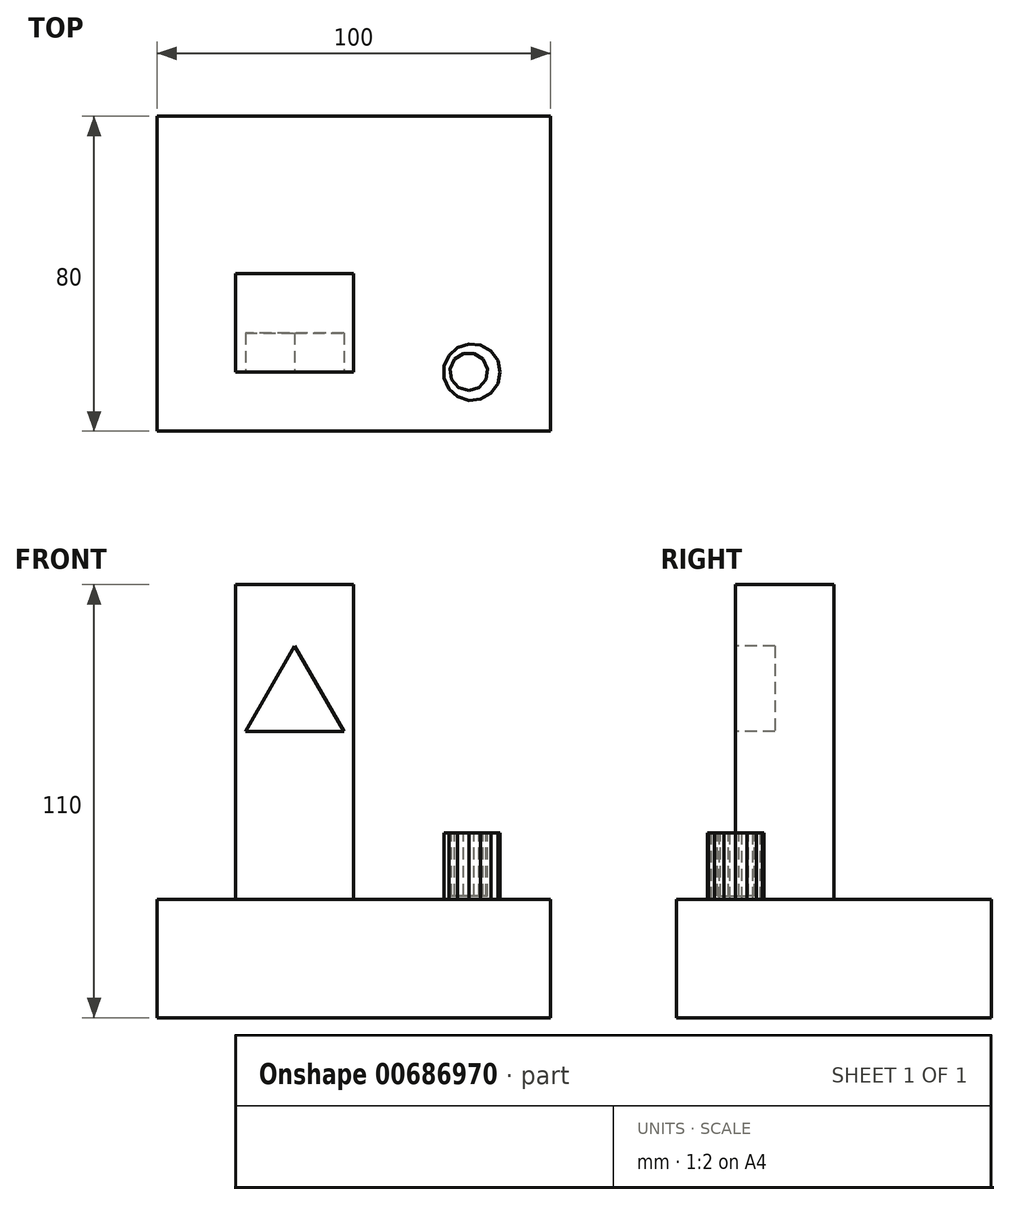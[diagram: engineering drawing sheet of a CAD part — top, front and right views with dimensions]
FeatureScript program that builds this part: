
annotation { "Feature Type Name" : "Feature", "Feature Type Description" : "" }
export const myFeature = defineFeature(function(context is Context, id is Id, definition is map)
    precondition{}
    {
        {
            var Q0;
            Q0=qCreatedBy(makeId("Top.planeOp"),FACE);
            var sketch = newSketch(context, id + "F0", { "sketchPlane" : qUnion([Q0])});
            skLineSegment(sketch, "E0.bottom", {"start": v(-50, 40) * mm, "end": v(50, 40) * mm});
            skLineSegment(sketch, "E0.top", {"start": v(-50, -40) * mm, "end": v(50, -40) * mm});
            skLineSegment(sketch, "E0.left", {"start": v(-50, 40) * mm, "end": v(-50, -40) * mm});
            skLineSegment(sketch, "E0.right", {"start": v(50, 40) * mm, "end": v(50, -40) * mm});
            skPoint(sketch, "E0.middle", {"position": v(0, 0) * mm});
            skSolve(sketch);
        }
        {
            var Q0;
            Q0=makeQuery(id+"F0.imprint","IMPRINT",FACE,{"disambiguationData":[TD([[makeQuery(id+"F0.imprint","IMPRINT",EDGE,{"derivedFrom":sQuery(id+"F0.wireOp",EDGE,"E0.bottom")}),-1.0]])]});
            extrude(context, id + "F1", {"entities" : qUnion([Q0]), "depth" : 30 * mm, "offsetDistance" : 25 * mm});
        }
        {
            var Q0;
            Q0=makeQuery(id+"F1.opExtrude","CAP_FACE",FACE,{"disambiguationData":[OSD([sQuery(id+"F0.wireOp",EDGE,"E0.bottom"),sQuery(id+"F0.wireOp",EDGE,"E0.top"),sQuery(id+"F0.wireOp",EDGE,"E0.left"),sQuery(id+"F0.wireOp",EDGE,"E0.right")])],"isStart":false});
            var sketch = newSketch(context, id + "F2", { "sketchPlane" : qUnion([Q0])});
            skLineSegment(sketch, "E1.bottom", {"start": v(-30, -25) * mm, "end": v(0, -25) * mm});
            skLineSegment(sketch, "E1.top", {"start": v(-30, 0) * mm, "end": v(0, 0) * mm});
            skLineSegment(sketch, "E1.left", {"start": v(-30, -25) * mm, "end": v(-30, 0) * mm});
            skLineSegment(sketch, "E1.right", {"start": v(0, -25) * mm, "end": v(0, 0) * mm});
            skSolve(sketch);
        }
        {
            var Q0;
            Q0=makeQuery(id+"F2.imprint","IMPRINT",FACE,{"disambiguationData":[TD([[makeQuery(id+"F2.imprint","IMPRINT",EDGE,{"derivedFrom":sQuery(id+"F2.wireOp",EDGE,"E1.bottom")}),1.0]])]});
            extrude(context, id + "F3", {"entities" : qUnion([Q0]), "operationType" : NewBodyOperationType.ADD, "depth" : 80 * mm, "offsetDistance" : 25 * mm});
        }
        {
            var Q0;
            Q0=makeQuery(id+"F3.opExtrude","SWEPT_FACE",FACE,{"disambiguationData":[OSD([sQuery(id+"F2.wireOp",EDGE,"E1.bottom")])]});
            var sketch = newSketch(context, id + "F4", { "sketchPlane" : qUnion([Q0])});
            skCircle(sketch, "E2.cCircle", {"center": v(-15, 80) * mm, "radius": 7.22 * mm, "construction": true});
            skLineSegment(sketch, "E2.0", {"start": v(-2.5, 72.78) * mm, "end": v(-27.5, 72.78) * mm});
            skLineSegment(sketch, "E2.1", {"start": v(-27.5, 72.78) * mm, "end": v(-15, 94.43) * mm});
            skLineSegment(sketch, "E2.2", {"start": v(-15, 94.43) * mm, "end": v(-2.5, 72.78) * mm});
            skPoint(sketch, "E2.0.midPoint", {"position": v(-15, 72.78) * mm});
            skSolve(sketch);
        }
        {
            var Q0;
            Q0=makeQuery(id+"F4.imprint","IMPRINT",FACE,{"disambiguationData":[TD([[makeQuery(id+"F4.imprint","IMPRINT",EDGE,{"derivedFrom":sQuery(id+"F4.wireOp",EDGE,"E2.0")}),-1.0]])]});
            extrude(context, id + "F5", {"entities" : qUnion([Q0]), "operationType" : NewBodyOperationType.REMOVE, "oppositeDirection" : true, "depth" : 10 * mm, "offsetDistance" : 25 * mm});
        }
        {
            var Q0;
            Q0=makeQuery(id+"F1.opExtrude","CAP_FACE",FACE,{"disambiguationData":[OSD([sQuery(id+"F0.wireOp",EDGE,"E0.bottom"),sQuery(id+"F0.wireOp",EDGE,"E0.top"),sQuery(id+"F0.wireOp",EDGE,"E0.left"),sQuery(id+"F0.wireOp",EDGE,"E0.right")])],"isStart":false});
            var sketch = newSketch(context, id + "F6", { "sketchPlane" : qUnion([Q0])});
            skCircle(sketch, "E3.cCircle", {"center": v(30, -25) * mm, "radius": 7.06 * mm, "construction": true});
            skLineSegment(sketch, "E3.0", {"start": v(22.94, -26.5) * mm, "end": v(22.94, -23.5) * mm});
            skLineSegment(sketch, "E3.1", {"start": v(22.94, -23.5) * mm, "end": v(24.16, -20.76) * mm});
            skLineSegment(sketch, "E3.2", {"start": v(24.16, -20.76) * mm, "end": v(26.4, -18.75) * mm});
            skLineSegment(sketch, "E3.3", {"start": v(26.4, -18.75) * mm, "end": v(29.25, -17.82) * mm});
            skLineSegment(sketch, "E3.4", {"start": v(29.25, -17.82) * mm, "end": v(32.23, -18.14) * mm});
            skLineSegment(sketch, "E3.5", {"start": v(32.23, -18.14) * mm, "end": v(34.83, -19.64) * mm});
            skLineSegment(sketch, "E3.6", {"start": v(34.83, -19.64) * mm, "end": v(36.6, -22.07) * mm});
            skLineSegment(sketch, "E3.7", {"start": v(36.6, -22.07) * mm, "end": v(37.21, -25) * mm});
            skLineSegment(sketch, "E3.8", {"start": v(37.21, -25) * mm, "end": v(36.6, -27.93) * mm});
            skLineSegment(sketch, "E3.9", {"start": v(36.6, -27.93) * mm, "end": v(34.83, -30.36) * mm});
            skLineSegment(sketch, "E3.10", {"start": v(34.83, -30.36) * mm, "end": v(32.23, -31.86) * mm});
            skLineSegment(sketch, "E3.11", {"start": v(32.23, -31.86) * mm, "end": v(29.25, -32.18) * mm});
            skLineSegment(sketch, "E3.12", {"start": v(29.25, -32.18) * mm, "end": v(26.4, -31.25) * mm});
            skLineSegment(sketch, "E3.13", {"start": v(26.4, -31.25) * mm, "end": v(24.16, -29.24) * mm});
            skLineSegment(sketch, "E3.14", {"start": v(24.16, -29.24) * mm, "end": v(22.94, -26.5) * mm});
            skPoint(sketch, "E3.0.midPoint", {"position": v(22.94, -25) * mm});
            skSolve(sketch);
        }
        {
            var Q0;
            Q0=makeQuery(id+"F6.imprint","IMPRINT",FACE,{"disambiguationData":[TD([[makeQuery(id+"F6.imprint","IMPRINT",EDGE,{"derivedFrom":sQuery(id+"F6.wireOp",EDGE,"E3.0")}),-1.0]])]});
            extrude(context, id + "F7", {"entities" : qUnion([Q0]), "operationType" : NewBodyOperationType.ADD, "depth" : 17 * mm, "offsetDistance" : 25 * mm});
        }
        {
            var Q0;
            Q0=makeQuery(id+"F7.opExtrude","CAP_FACE",FACE,{"disambiguationData":[OSD([sQuery(id+"F6.wireOp",EDGE,"E3.0"),sQuery(id+"F6.wireOp",EDGE,"E3.1"),sQuery(id+"F6.wireOp",EDGE,"E3.2"),sQuery(id+"F6.wireOp",EDGE,"E3.3"),sQuery(id+"F6.wireOp",EDGE,"E3.4"),sQuery(id+"F6.wireOp",EDGE,"E3.5"),sQuery(id+"F6.wireOp",EDGE,"E3.6"),sQuery(id+"F6.wireOp",EDGE,"E3.7"),sQuery(id+"F6.wireOp",EDGE,"E3.8"),sQuery(id+"F6.wireOp",EDGE,"E3.9"),sQuery(id+"F6.wireOp",EDGE,"E3.10"),sQuery(id+"F6.wireOp",EDGE,"E3.11"),sQuery(id+"F6.wireOp",EDGE,"E3.12"),sQuery(id+"F6.wireOp",EDGE,"E3.13"),sQuery(id+"F6.wireOp",EDGE,"E3.14")])],"isStart":false});
            var sketch = newSketch(context, id + "F8", { "sketchPlane" : qUnion([Q0])});
            skCircle(sketch, "E4.cCircle", {"center": v(29.25, -24.82) * mm, "radius": 4.6 * mm, "construction": true});
            skLineSegment(sketch, "E4.0", {"start": v(24.5, -24.14) * mm, "end": v(25.62, -21.69) * mm});
            skLineSegment(sketch, "E4.1", {"start": v(25.62, -21.69) * mm, "end": v(27.9, -20.23) * mm});
            skLineSegment(sketch, "E4.2", {"start": v(27.9, -20.23) * mm, "end": v(30.6, -20.23) * mm});
            skLineSegment(sketch, "E4.3", {"start": v(30.6, -20.23) * mm, "end": v(32.87, -21.69) * mm});
            skLineSegment(sketch, "E4.4", {"start": v(32.87, -21.69) * mm, "end": v(33.99, -24.14) * mm});
            skLineSegment(sketch, "E4.5", {"start": v(33.99, -24.14) * mm, "end": v(33.6, -26.82) * mm});
            skLineSegment(sketch, "E4.6", {"start": v(33.6, -26.82) * mm, "end": v(31.84, -28.86) * mm});
            skLineSegment(sketch, "E4.7", {"start": v(31.84, -28.86) * mm, "end": v(29.25, -29.62) * mm});
            skLineSegment(sketch, "E4.8", {"start": v(29.25, -29.62) * mm, "end": v(26.66, -28.86) * mm});
            skLineSegment(sketch, "E4.9", {"start": v(26.66, -28.86) * mm, "end": v(24.89, -26.82) * mm});
            skLineSegment(sketch, "E4.10", {"start": v(24.89, -26.82) * mm, "end": v(24.5, -24.14) * mm});
            skPoint(sketch, "E4.0.midPoint", {"position": v(25.06, -22.91) * mm});
            skSolve(sketch);
        }
        {
            var Q0;
            Q0=makeQuery(id+"F8.imprint","IMPRINT",FACE,{"disambiguationData":[TD([[makeQuery(id+"F8.imprint","IMPRINT",EDGE,{"derivedFrom":sQuery(id+"F8.wireOp",EDGE,"E4.0")}),-1.0]])]});
            extrude(context, id + "F9", {"entities" : qUnion([Q0]), "operationType" : NewBodyOperationType.REMOVE, "oppositeDirection" : true, "depth" : 16 * mm, "offsetDistance" : 25 * mm});
        }
    });
